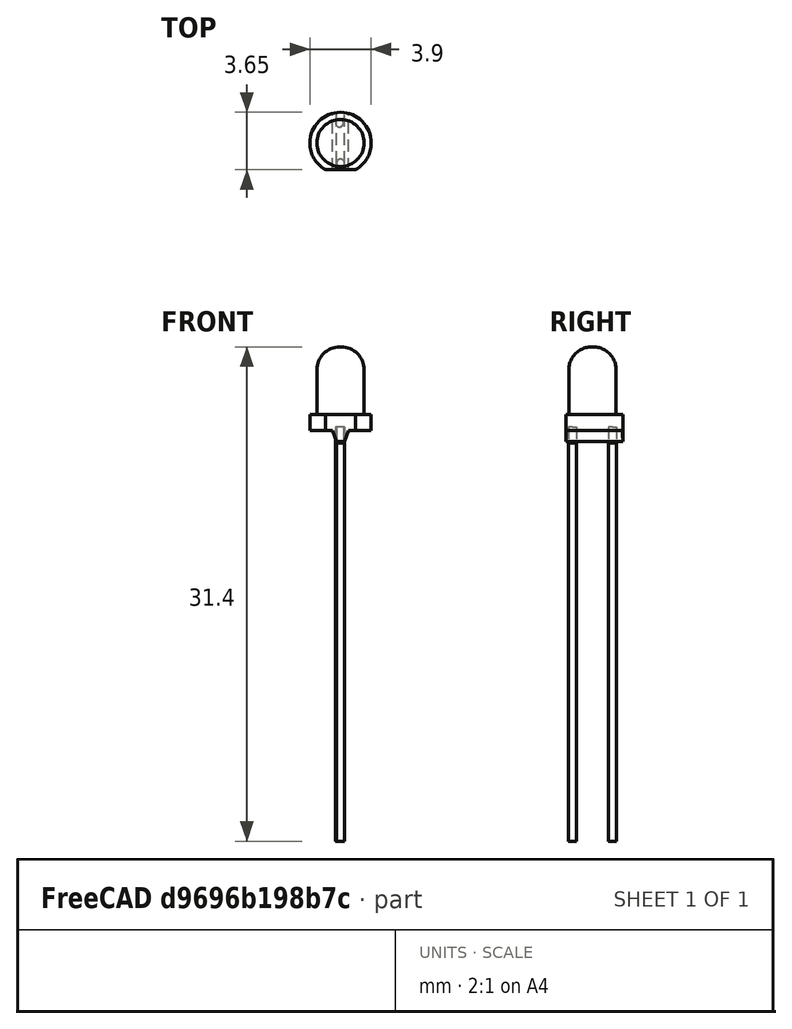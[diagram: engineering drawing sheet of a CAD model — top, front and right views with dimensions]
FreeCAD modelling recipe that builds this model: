
FCSTD DOCUMENT  (FreeCAD 0.14R3702 (Git))
Label: led3mm
License: CC-BY 3.0
LicenseURL: http://creativecommons.org/licenses/by/3.0/
objects: Part::Feature×2, Part::Box×2, Part::Cut×1, Part::MultiCommon×1, App::DocumentObjectGroup×1
note: 6 computed .brp shape members not serialized (recipe doc carries the construction recipe); baked Part::Feature solids carry a one-line shape summary decoded from their .brp

FEATURE [Part::Feature] Part__Feature  label="led3mm002"
  shape: bbox 3.9 x 3.646 x 32.4 mm, 23 faces (baked)
FEATURE [Part::Box] Box  label="Cube"
  Height = 10
  Length = 10
  Placement = pos=(-5,-3,-1.8) rot=(0,0,1;0rad)
  Width = 10
FEATURE [Part::Feature] Part__Feature001  label="led3mm001"
  shape: bbox 3.9 x 3.646 x 32.4 mm, 23 faces (baked)
FEATURE [Part::Box] Box001  label="Cube001"
  Height = 10
  Length = 10
  Placement = pos=(-5,-3,-1.8) rot=(0,0,1;0rad)
  Width = 10
FEATURE [Part::Cut] Cut
  Base = -> Part__Feature
  Placement = pos=(0,0,1) rot=(0,0,1;0rad)
  Tool = -> Box
FEATURE [Part::MultiCommon] Common
  Shapes = -> [Part__Feature001,Box001]
FEATURE [App::DocumentObjectGroup] Group  label="led3mm"
  Group = -> [Common,Cut]
